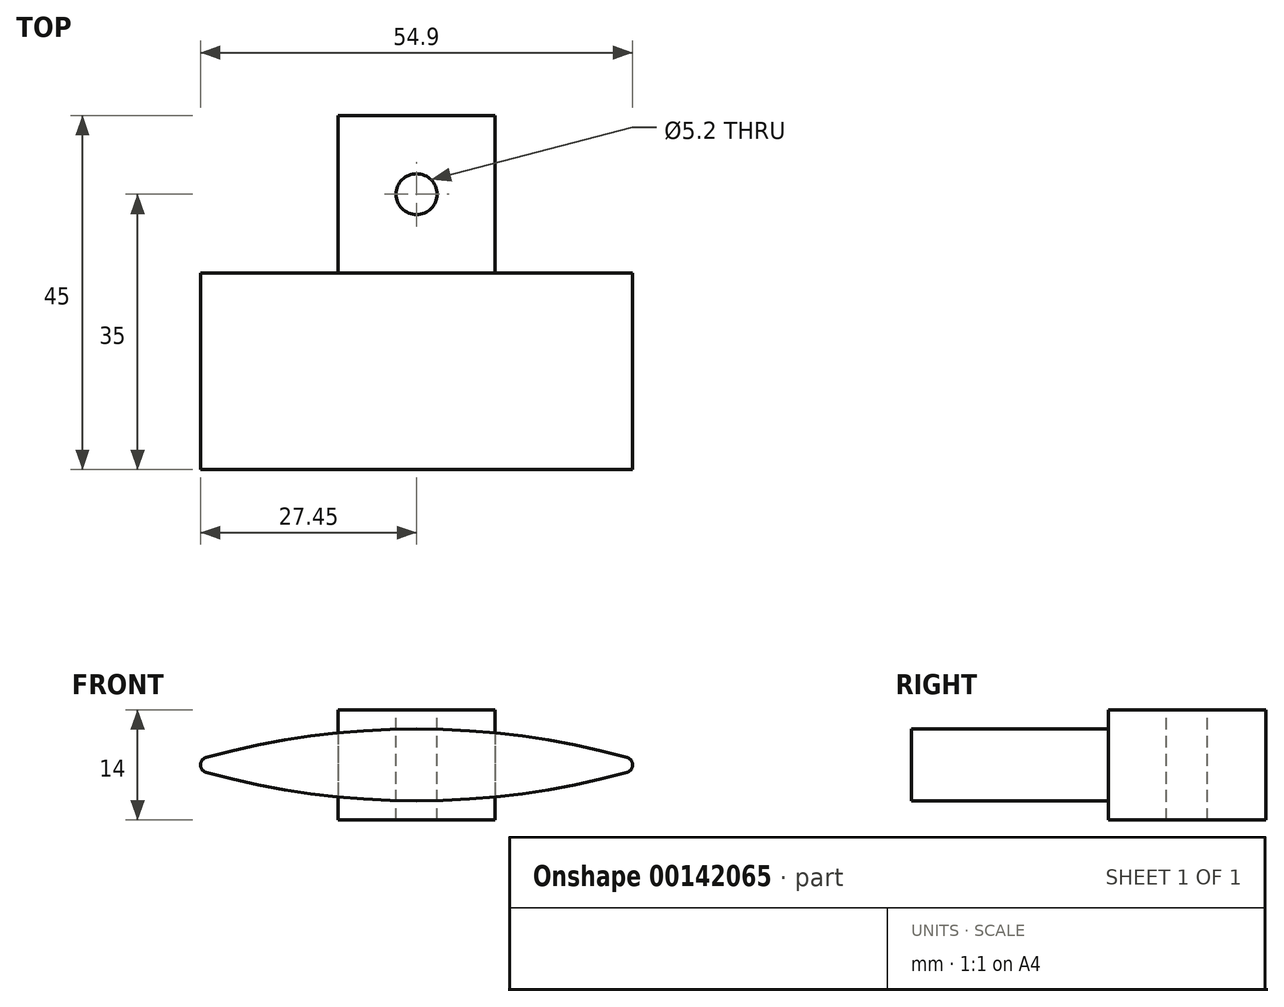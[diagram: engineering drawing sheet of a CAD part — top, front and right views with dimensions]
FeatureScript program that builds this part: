
annotation { "Feature Type Name" : "Feature", "Feature Type Description" : "" }
export const myFeature = defineFeature(function(context is Context, id is Id, definition is map)
    precondition{}
    {
        {
            var Q0;
            Q0=qCreatedBy(makeId("Top.planeOp"),FACE);
            var sketch = newSketch(context, id + "F0", { "sketchPlane" : qUnion([Q0])});
            skLineSegment(sketch, "E0.bottom", {"start": v(0, 0) * mm, "end": v(20, 0) * mm});
            skLineSegment(sketch, "E0.top", {"start": v(0, 20) * mm, "end": v(20, 20) * mm});
            skLineSegment(sketch, "E0.left", {"start": v(0, 0) * mm, "end": v(0, 20) * mm});
            skLineSegment(sketch, "E0.right", {"start": v(20, 0) * mm, "end": v(20, 20) * mm});
            skSolve(sketch);
        }
        {
            var Q0;
            Q0=makeQuery(id+"F0.imprint","IMPRINT",FACE,{"disambiguationData":[TD([[makeQuery(id+"F0.imprint","IMPRINT",EDGE,{"derivedFrom":sQuery(id+"F0.wireOp",EDGE,"E0.bottom")}),1.0]])]});
            extrude(context, id + "F1", {"entities" : qUnion([Q0]), "depth" : 14 * mm});
        }
        {
            var Q0;
            Q0=qCreatedBy(makeId("Front.planeOp"),FACE);
            var sketch = newSketch(context, id + "F2", { "sketchPlane" : qUnion([Q0])});
            skArc(sketch, "E1", {"start": v(40, 7) * mm, "mid": v(10, 11.57) * mm, "end": v(-20, 7) * mm});
            skArc(sketch, "E2.MirrorCS", {"start": v(40, 7) * mm, "mid": v(10, 2.43) * mm, "end": v(-20, 7) * mm});
            skSolve(sketch);
        }
        {
            var Q0;
            Q0=makeQuery(id+"F2.imprint","IMPRINT",FACE,{"disambiguationData":[TD([[makeQuery(id+"F2.imprint","IMPRINT",EDGE,{"derivedFrom":sQuery(id+"F2.wireOp",EDGE,"E1")}),1.0]])]});
            extrude(context, id + "F3", {"entities" : qUnion([Q0]), "operationType" : NewBodyOperationType.ADD, "depth" : 25 * mm});
        }
        {
            var Q0;
            Q0=makeQuery(id+"F1.opExtrude","CAP_FACE",FACE,{"disambiguationData":[OSD([sQuery(id+"F0.wireOp",EDGE,"E0.bottom"),sQuery(id+"F0.wireOp",EDGE,"E0.top"),sQuery(id+"F0.wireOp",EDGE,"E0.left"),sQuery(id+"F0.wireOp",EDGE,"E0.right")])],"isStart":false});
            var sketch = newSketch(context, id + "F4", { "sketchPlane" : qUnion([Q0])});
            skLineSegment(sketch, "E3", {"start": v(0, 20) * mm, "end": v(20, 0) * mm, "construction": true});
            skLineSegment(sketch, "E4", {"start": v(20, 20) * mm, "end": v(0, 0) * mm, "construction": true});
            skCircle(sketch, "E5", {"center": v(10, 10) * mm, "radius": 2.6 * mm, "construction": true});
            skCircle(sketch, "E6", {"center": v(0, 10) * mm, "radius": 1.02 * mm, "construction": true});
            skSolve(sketch);
        }
        {
            var Q0;
            Q0=sQuery(id+"F4.wireOp",VERTEX,"E5.center");
            var Q1;
            Q1=makeQuery(id+"F1.opExtrude","SWEPT_BODY",BODY,{"disambiguationData":[OSD([sQuery(id+"F0.wireOp",EDGE,"E0.bottom"),sQuery(id+"F0.wireOp",EDGE,"E0.top"),sQuery(id+"F0.wireOp",EDGE,"E0.left"),sQuery(id+"F0.wireOp",EDGE,"E0.right")])]});
            hole(context, id + "F5", {"style" : HoleStyle.SIMPLE, "endStyle" : HoleEndStyle.THROUGH, "holeDiameter" : 5.2 * mm, "locations" : qUnion([Q0]), "scope" : qUnion([Q1]), "isTappedThrough" : true});
        }
        {
            var Q0;
            {var subQ0=sQuery(id+"F2.wireOp",EDGE,"E2.MirrorCS");var subQ1=sQuery(id+"F2.wireOp",EDGE,"E1");Q0=makeQuery(id+"F3.opExtrude","SWEPT_EDGE",EDGE,{"disambiguationData":[OSD([subQ1,subQ0]),TDD([makeQuery(id+"F2.imprint","INTERSECT",VERTEX,{"disambiguationData":[OD(0.0)],"derivedFrom":[subQ1,subQ0]})])]});}
            fillet(context, id + "F6", {"entities" : qUnion([Q0]), "radius" : 1 * mm, "tangentPropagation" : true, "allowEdgeOverflow" : false});
        }
        {
            var Q0;
            {var subQ0=sQuery(id+"F2.wireOp",EDGE,"E2.MirrorCS");var subQ1=sQuery(id+"F2.wireOp",EDGE,"E1");Q0=makeQuery(id+"F3.opExtrude","SWEPT_EDGE",EDGE,{"disambiguationData":[OSD([subQ1,subQ0]),TDD([makeQuery(id+"F2.imprint","INTERSECT",VERTEX,{"disambiguationData":[OD(1.0)],"derivedFrom":[subQ1,subQ0]})])]});}
            fillet(context, id + "F7", {"entities" : qUnion([Q0]), "radius" : 1 * mm, "tangentPropagation" : true, "allowEdgeOverflow" : false});
        }
    });
